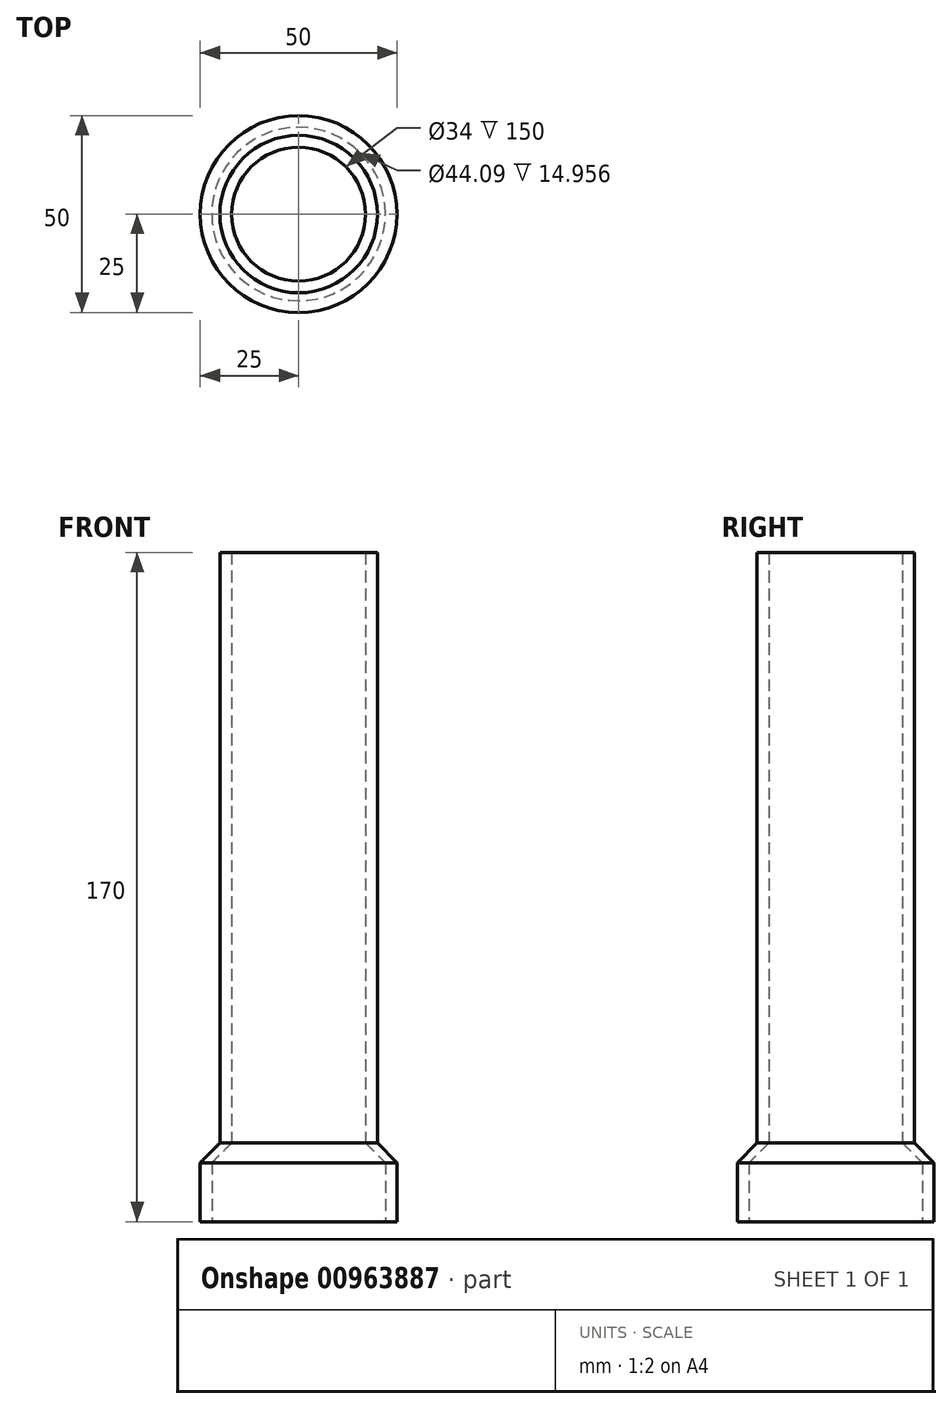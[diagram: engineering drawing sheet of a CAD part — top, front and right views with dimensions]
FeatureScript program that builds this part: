
annotation { "Feature Type Name" : "Feature", "Feature Type Description" : "" }
export const myFeature = defineFeature(function(context is Context, id is Id, definition is map)
    precondition{}
    {
        {
            var Q0;
            Q0=qCreatedBy(makeId("Front.planeOp"),FACE);
            var sketch = newSketch(context, id + "F0", { "sketchPlane" : qUnion([Q0])});
            skLineSegment(sketch, "E0", {"start": v(25, 0) * mm, "end": v(25, 15) * mm});
            skLineSegment(sketch, "E1", {"start": v(20, 170) * mm, "end": v(20, 20) * mm});
            skLineSegment(sketch, "E2.0", {"start": v(22.04, 0) * mm, "end": v(22.04, 14.96) * mm});
            skLineSegment(sketch, "E2.2", {"start": v(17, 170) * mm, "end": v(17, 20) * mm});
            skLineSegment(sketch, "E3", {"start": v(17, 170) * mm, "end": v(20, 170) * mm});
            skLineSegment(sketch, "E4", {"start": v(22.04, 0) * mm, "end": v(25, 0) * mm});
            skLineSegment(sketch, "E5", {"start": v(0, 0) * mm, "end": v(0, 91.6) * mm, "construction": true});
            skLineSegment(sketch, "E6", {"start": v(20, 20) * mm, "end": v(25, 15) * mm});
            skLineSegment(sketch, "E7", {"start": v(17, 20) * mm, "end": v(22.04, 14.96) * mm});
            skSolve(sketch);
        }
        {
            var Q0;
            Q0=makeQuery(id+"F0.imprint","IMPRINT",FACE,{"disambiguationData":[TD([[makeQuery(id+"F0.imprint","IMPRINT",EDGE,{"derivedFrom":sQuery(id+"F0.wireOp",EDGE,"E0")}),1.0]])]});
            var Q1;
            Q1=sQuery(id+"F0.wireOp",EDGE,"E5");
            revolve(context, id + "F1", {"surfaceOperationType" : NewSurfaceOperationType.NEW, "entities" : qUnion([Q0]), "axis" : qUnion([Q1]), "revolveType" : RevolveType.FULL});
        }
    });
